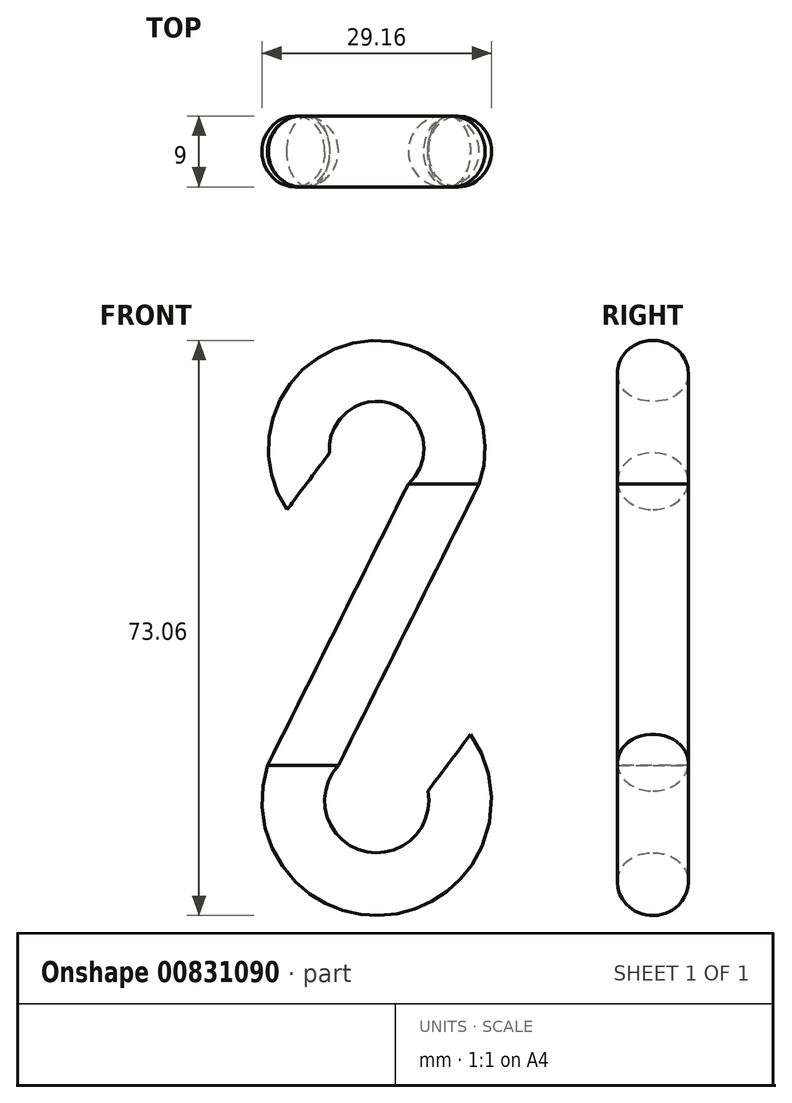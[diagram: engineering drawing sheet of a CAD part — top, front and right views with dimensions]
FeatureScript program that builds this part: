
annotation { "Feature Type Name" : "Feature", "Feature Type Description" : "" }
export const myFeature = defineFeature(function(context is Context, id is Id, definition is map)
    precondition{}
    {
        {
            var Q0;
            Q0=qCreatedBy(makeId("Front.planeOp"),FACE);
            var sketch = newSketch(context, id + "F0", { "sketchPlane" : qUnion([Q0])});
            skArc(sketch, "E0", {"start": v(-8.94, -9.75) * mm, "mid": v(0, -24.22) * mm, "end": v(8.94, -9.75) * mm});
            skArc(sketch, "E1", {"start": v(-8.94, 26.03) * mm, "mid": v(0, 40.5) * mm, "end": v(8.94, 26.03) * mm});
            skLineSegment(sketch, "E2", {"start": v(8.94, 26.03) * mm, "end": v(-8.94, -9.75) * mm});
            skLineSegment(sketch, "E3", {"start": v(-8.94, -9.75) * mm, "end": v(26.33, -9.75) * mm, "construction": true});
            skLineSegment(sketch, "E4", {"start": v(8.94, 26.03) * mm, "end": v(-24.34, 26.03) * mm, "construction": true});
            skPoint(sketch, "E5", {"position": v(-4.07, 0) * mm});
            skSolve(sketch);
        }
        {
            var Q0;
            Q0=qCreatedBy(makeId("Top.planeOp"),FACE);
            var sketch = newSketch(context, id + "F1", { "sketchPlane" : qUnion([Q0])});
            skCircle(sketch, "E6", {"center": v(-4.5, 0) * mm, "radius": 4.5 * mm});
            skSolve(sketch);
        }
        {
            var Q0;
            Q0=makeQuery(id+"F1.imprint","IMPRINT",FACE,{"disambiguationData":[TD([[makeQuery(id+"F1.imprint","IMPRINT",EDGE,{"derivedFrom":sQuery(id+"F1.wireOp",EDGE,"E6")}),1.0]])]});
            var Q1;
            Q1=sQuery(id+"F0.wireOp",EDGE,"E0");
            var Q2;
            Q2=sQuery(id+"F0.wireOp",EDGE,"E2");
            var Q3;
            Q3=sQuery(id+"F0.wireOp",EDGE,"E1");
            sweep(context, id + "F2", {"profiles" : qUnion([Q0]), "path" : qUnion([Q1, Q2, Q3])});
        }
    });
